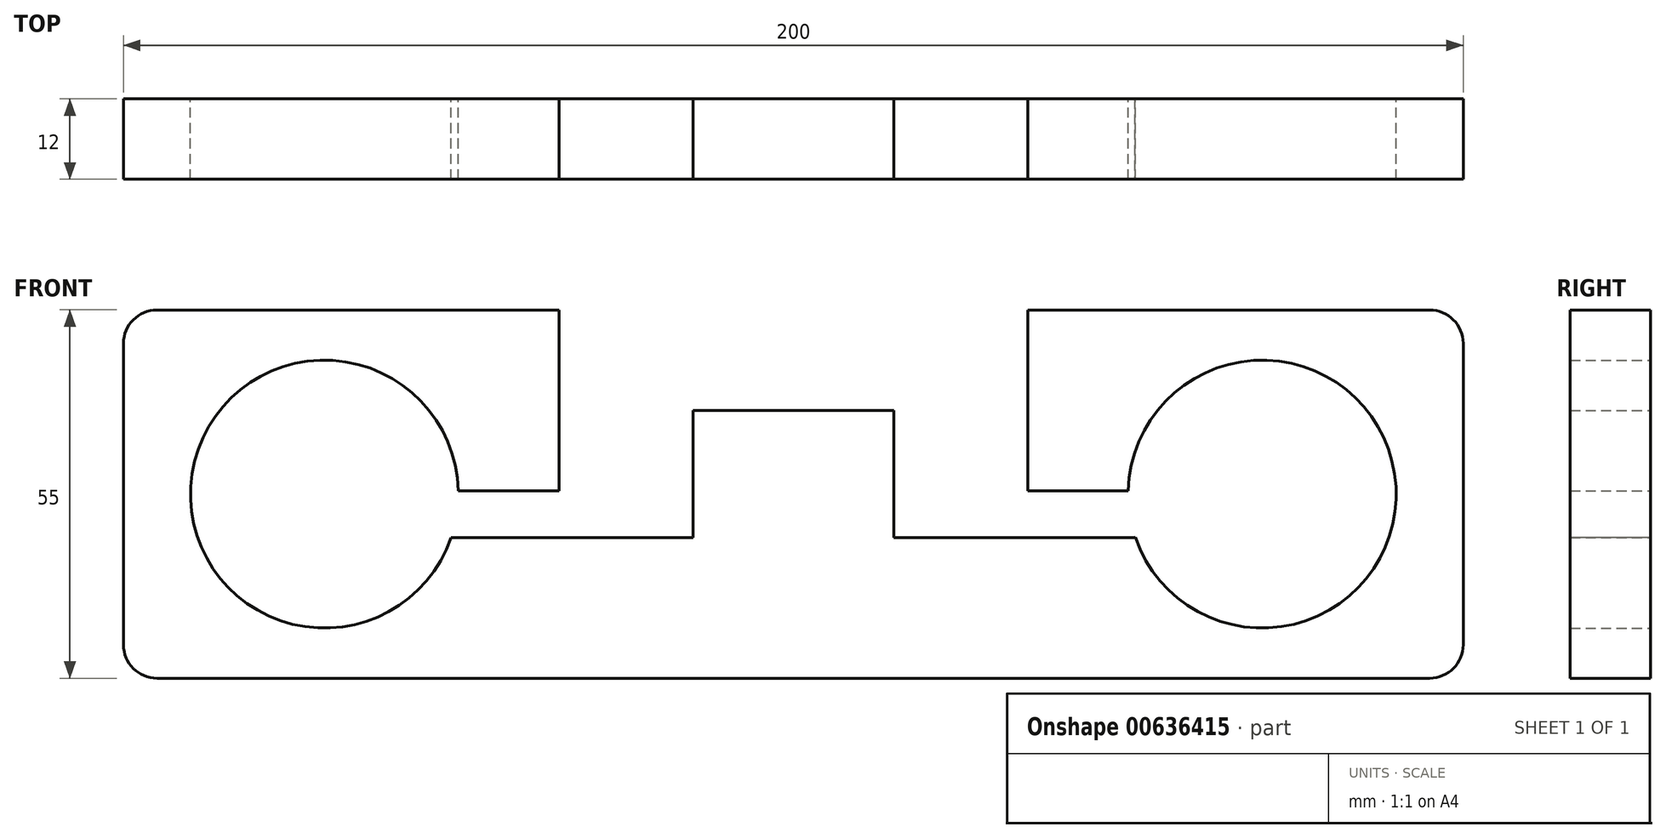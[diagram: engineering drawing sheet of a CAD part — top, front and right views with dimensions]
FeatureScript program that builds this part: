
annotation { "Feature Type Name" : "Feature", "Feature Type Description" : "" }
export const myFeature = defineFeature(function(context is Context, id is Id, definition is map)
    precondition{}
    {
        {
            var Q0;
            Q0=qCreatedBy(makeId("Front.planeOp"),FACE);
            var sketch = newSketch(context, id + "F0", { "sketchPlane" : qUnion([Q0])});
            skLineSegment(sketch, "E0.bottom", {"start": v(-79.88, 47.92) * mm, "end": v(110.12, 47.92) * mm});
            skLineSegment(sketch, "E0.top", {"start": v(-79.88, -7.08) * mm, "end": v(110.12, -7.08) * mm});
            skLineSegment(sketch, "E0.left", {"start": v(-84.88, 42.92) * mm, "end": v(-84.88, -2.08) * mm});
            skLineSegment(sketch, "E0.right", {"start": v(115.12, 42.92) * mm, "end": v(115.12, -2.08) * mm});
            skPoint(sketch, "E1.visualSharp", {"position": v(-84.88, 47.92) * mm});
            skArc(sketch, "E1.filletArc", {"start": v(-79.88, 47.92) * mm, "mid": v(-83.41, 46.45) * mm, "end": v(-84.88, 42.92) * mm});
            skPoint(sketch, "E2.visualSharp", {"position": v(115.12, 47.92) * mm});
            skArc(sketch, "E2.filletArc", {"start": v(115.12, 42.92) * mm, "mid": v(113.66, 46.45) * mm, "end": v(110.12, 47.92) * mm});
            skPoint(sketch, "E3.visualSharp", {"position": v(115.12, -7.08) * mm});
            skArc(sketch, "E3.filletArc", {"start": v(110.12, -7.08) * mm, "mid": v(113.66, -5.62) * mm, "end": v(115.12, -2.08) * mm});
            skPoint(sketch, "E4.visualSharp", {"position": v(-84.88, -7.08) * mm});
            skArc(sketch, "E4.filletArc", {"start": v(-84.88, -2.08) * mm, "mid": v(-83.41, -5.62) * mm, "end": v(-79.88, -7.08) * mm});
            skCircle(sketch, "E5", {"center": v(-54.88, 20.42) * mm, "radius": 20 * mm});
            skCircle(sketch, "E6", {"center": v(85.12, 20.42) * mm, "radius": 20 * mm});
            skSolve(sketch);
        }
        {
            var Q0;
            Q0=makeQuery(id+"F0.imprint","IMPRINT",FACE,{"disambiguationData":[TD([[makeQuery(id+"F0.imprint","IMPRINT",EDGE,{"derivedFrom":sQuery(id+"F0.wireOp",EDGE,"E0.bottom")}),-1.0]])]});
            extrude(context, id + "F1", {"entities" : qUnion([Q0]), "depth" : 12 * mm, "offsetDistance" : 25 * mm});
        }
        {
            var Q0;
            Q0=makeQuery(id+"F1.opExtrude","CAP_FACE",FACE,{"disambiguationData":[OSD([sQuery(id+"F0.wireOp",EDGE,"E0.bottom"),sQuery(id+"F0.wireOp",EDGE,"E0.top"),sQuery(id+"F0.wireOp",EDGE,"E0.left"),sQuery(id+"F0.wireOp",EDGE,"E0.right"),sQuery(id+"F0.wireOp",EDGE,"E1.filletArc"),sQuery(id+"F0.wireOp",EDGE,"E2.filletArc"),sQuery(id+"F0.wireOp",EDGE,"E3.filletArc"),sQuery(id+"F0.wireOp",EDGE,"E4.filletArc"),sQuery(id+"F0.wireOp",EDGE,"E5"),sQuery(id+"F0.wireOp",EDGE,"E6")])],"isStart":false});
            var sketch = newSketch(context, id + "F2", { "sketchPlane" : qUnion([Q0])});
            skLineSegment(sketch, "E7", {"start": v(-19.88, 47.92) * mm, "end": v(-19.88, 73.58) * mm});
            skLineSegment(sketch, "E8", {"start": v(50.12, 47.92) * mm, "end": v(50.12, 77.54) * mm});
            skSolve(sketch);
        }
        {
            var Q0;
            Q0=makeQuery(id+"F1.opExtrude","SWEPT_FACE",FACE,{"disambiguationData":[OSD([sQuery(id+"F0.wireOp",EDGE,"E0.bottom")])]});
            var sketch = newSketch(context, id + "F3", { "sketchPlane" : qUnion([Q0])});
            skLineSegment(sketch, "E9", {"start": v(-19.88, -12) * mm, "end": v(-19.88, 0) * mm});
            skLineSegment(sketch, "E10", {"start": v(50.12, -12) * mm, "end": v(50.12, 0) * mm});
            skSolve(sketch);
        }
        {
            var Q0;
            {var subQ0=sQuery(id+"F3.wireOp",EDGE,"E9");Q0=makeQuery(id+"F3.imprint","IMPRINT",FACE,{"disambiguationData":[TD([[makeQuery(id+"F3.imprint","IMPRINT",EDGE,{"derivedFrom":subQ0}),-1.0]])]});}
            extrude(context, id + "F4", {"entities" : qUnion([Q0]), "operationType" : NewBodyOperationType.REMOVE, "oppositeDirection" : true, "depth" : 15 * mm, "offsetDistance" : 25 * mm});
        }
        {
            var Q0;
            Q0=makeQuery(id+"F4.boolean.opBoolean","COPY",FACE,{"derivedFrom":makeQuery(id+"F4.opExtrude","CAP_FACE",FACE,{"disambiguationData":[OSD([sQuery(id+"F0.wireOp",EDGE,"E0.bottom"),sQuery(id+"F3.wireOp",EDGE,"E9"),sQuery(id+"F3.wireOp",EDGE,"E10")])],"isStart":false})});
            var sketch = newSketch(context, id + "F5", { "sketchPlane" : qUnion([Q0])});
            skLineSegment(sketch, "E11", {"start": v(0.12, -12) * mm, "end": v(0.12, 0) * mm});
            skLineSegment(sketch, "E12", {"start": v(30.12, 0) * mm, "end": v(30.12, -12) * mm});
            skSolve(sketch);
        }
        {
            var Q0;
            {var subQ0=sQuery(id+"F5.wireOp",EDGE,"E11");Q0=makeQuery(id+"F5.imprint","IMPRINT",FACE,{"disambiguationData":[TD([[makeQuery(id+"F5.imprint","IMPRINT",EDGE,{"derivedFrom":subQ0}),1.0]])]});}
            var Q1;
            {var subQ0=sQuery(id+"F5.wireOp",EDGE,"E12");Q1=makeQuery(id+"F5.imprint","IMPRINT",FACE,{"disambiguationData":[TD([[makeQuery(id+"F5.imprint","IMPRINT",EDGE,{"derivedFrom":subQ0}),1.0]])]});}
            extrude(context, id + "F6", {"entities" : qUnion([Q0, Q1]), "operationType" : NewBodyOperationType.REMOVE, "oppositeDirection" : true, "depth" : 12 * mm, "offsetDistance" : 25 * mm});
        }
        {
            var Q0;
            Q0=makeQuery(id+"F2.imprint","IMPRINT",FACE,{"disambiguationData":[TD([[makeQuery(id+"F2.imprint","IMPRINT",EDGE,{"derivedFrom":makeQuery(id+"F1.opExtrude","CAP_EDGE",EDGE,{"disambiguationData":[OSD([sQuery(id+"F0.wireOp",EDGE,"E0.top")])],"isStart":false})}),1.0]])]});
            var sketch = newSketch(context, id + "F7", { "sketchPlane" : qUnion([Q0])});
            skLineSegment(sketch, "E13", {"start": v(-19.86, 20.93) * mm, "end": v(-34.91, 20.93) * mm});
            skLineSegment(sketch, "E14", {"start": v(0.13, 20.94) * mm, "end": v(0.13, 13.94) * mm});
            skLineSegment(sketch, "E15", {"start": v(0.13, 13.94) * mm, "end": v(-36.02, 13.94) * mm});
            skLineSegment(sketch, "E16", {"start": v(50.12, 20.93) * mm, "end": v(65.14, 20.93) * mm});
            skLineSegment(sketch, "E17", {"start": v(30.12, 20.92) * mm, "end": v(30.12, 13.93) * mm});
            skLineSegment(sketch, "E18", {"start": v(30.12, 13.93) * mm, "end": v(66.08, 13.93) * mm});
            skLineSegment(sketch, "E19", {"start": v(-19.86, 20.93) * mm, "end": v(0.13, 20.94) * mm});
            skLineSegment(sketch, "E20", {"start": v(30.12, 20.92) * mm, "end": v(50.12, 20.93) * mm});
            skLineSegment(sketch, "E21", {"start": v(65.14, 20.93) * mm, "end": v(73.13, 16.83) * mm});
            skLineSegment(sketch, "E22", {"start": v(73.13, 16.83) * mm, "end": v(66.08, 13.93) * mm});
            skLineSegment(sketch, "E23", {"start": v(-34.91, 20.93) * mm, "end": v(-38.79, 20.93) * mm});
            skLineSegment(sketch, "E24", {"start": v(-38.79, 20.93) * mm, "end": v(-36.02, 13.94) * mm});
            skSolve(sketch);
        }
        {
            var Q0;
            Q0 = qSketchRegion(id + "F7", true);
            extrude(context, id + "F8", {"entities" : qUnion([Q0]), "operationType" : NewBodyOperationType.REMOVE, "oppositeDirection" : true, "depth" : 25 * mm, "offsetDistance" : 25 * mm});
        }
    });
